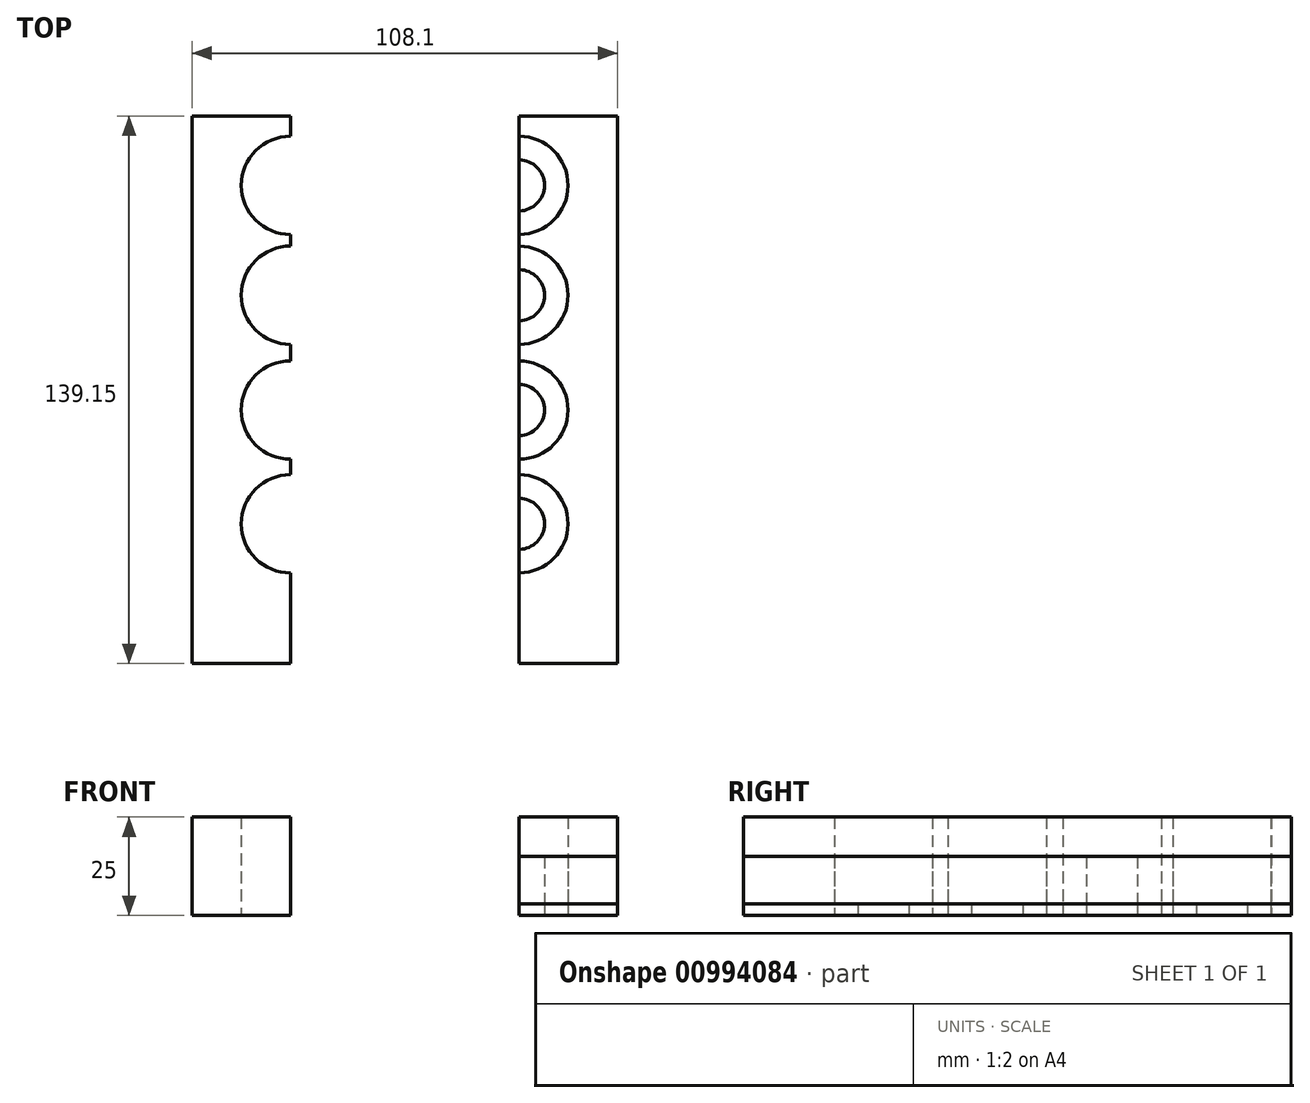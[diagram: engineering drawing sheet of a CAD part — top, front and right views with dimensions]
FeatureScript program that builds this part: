
annotation { "Feature Type Name" : "Feature", "Feature Type Description" : "" }
export const myFeature = defineFeature(function(context is Context, id is Id, definition is map)
    precondition{}
    {
        {
            var Q0;
            Q0=qCreatedBy(makeId("Top.planeOp"),FACE);
            var sketch = newSketch(context, id + "F0", { "sketchPlane" : qUnion([Q0])});
            skLineSegment(sketch, "E0.bottom", {"start": v(-54, 72.63) * mm, "end": v(54.1, 72.63) * mm});
            skLineSegment(sketch, "E0.top", {"start": v(-54, -66.52) * mm, "end": v(54.1, -66.52) * mm});
            skLineSegment(sketch, "E0.left", {"start": v(-54, 72.63) * mm, "end": v(-54, -66.52) * mm});
            skLineSegment(sketch, "E0.right", {"start": v(54.1, 72.63) * mm, "end": v(54.1, -66.52) * mm});
            skLineSegment(sketch, "E1.bottom", {"start": v(-54, 72.63) * mm, "end": v(-29, 72.63) * mm});
            skLineSegment(sketch, "E1.top", {"start": v(-54, -66.52) * mm, "end": v(-29, -66.52) * mm});
            skLineSegment(sketch, "E1.right", {"start": v(-29, 72.63) * mm, "end": v(-29, -66.52) * mm});
            skLineSegment(sketch, "E2.bottom", {"start": v(-29, 72.63) * mm, "end": v(0, 72.63) * mm});
            skLineSegment(sketch, "E2.top", {"start": v(-29, -66.52) * mm, "end": v(0, -66.52) * mm});
            skLineSegment(sketch, "E2.right", {"start": v(0, 72.63) * mm, "end": v(0, -66.52) * mm});
            skLineSegment(sketch, "E3.bottom", {"start": v(0, 72.63) * mm, "end": v(29.1, 72.63) * mm});
            skLineSegment(sketch, "E3.top", {"start": v(0, -66.52) * mm, "end": v(29.1, -66.52) * mm});
            skLineSegment(sketch, "E3.right", {"start": v(29.1, 72.63) * mm, "end": v(29.1, -66.52) * mm});
            skCircle(sketch, "E4", {"center": v(-29, 55) * mm, "radius": 12.5 * mm});
            skCircle(sketch, "E5", {"center": v(-29, 27.08) * mm, "radius": 12.5 * mm});
            skCircle(sketch, "E6", {"center": v(-29, -2.09) * mm, "radius": 12.5 * mm});
            skCircle(sketch, "E7", {"center": v(-29, -30.99) * mm, "radius": 12.5 * mm});
            skLineSegment(sketch, "E8.MirrorCS", {"start": v(0, 73.48) * mm, "end": v(0, -66.52) * mm});
            skCircle(sketch, "E9.MirrorC", {"center": v(29, 55) * mm, "radius": 12.5 * mm});
            skCircle(sketch, "E10.MirrorC", {"center": v(29, 27.08) * mm, "radius": 12.5 * mm});
            skCircle(sketch, "E11.MirrorC", {"center": v(29, -2.09) * mm, "radius": 12.5 * mm});
            skCircle(sketch, "E12.MirrorC", {"center": v(29, -30.99) * mm, "radius": 12.5 * mm});
            skCircle(sketch, "E13.MirrorC", {"center": v(0, 55) * mm, "radius": 12.5 * mm});
            skCircle(sketch, "E14.MirrorC", {"center": v(0, 27.08) * mm, "radius": 12.5 * mm});
            skCircle(sketch, "E15.MirrorC", {"center": v(0, -2.09) * mm, "radius": 12.5 * mm});
            skCircle(sketch, "E16.MirrorC", {"center": v(0, -30.99) * mm, "radius": 12.5 * mm});
            skCircle(sketch, "E17", {"center": v(-29, 55) * mm, "radius": 6.5 * mm});
            skCircle(sketch, "E18", {"center": v(-29, 27.08) * mm, "radius": 6.5 * mm});
            skCircle(sketch, "E19", {"center": v(-29, -2.09) * mm, "radius": 6.5 * mm});
            skCircle(sketch, "E20", {"center": v(-29, -30.99) * mm, "radius": 6.5 * mm});
            skCircle(sketch, "E21", {"center": v(0, -2.09) * mm, "radius": 6.5 * mm});
            skCircle(sketch, "E22", {"center": v(0, -30.99) * mm, "radius": 6.5 * mm});
            skCircle(sketch, "E23", {"center": v(0, 27.08) * mm, "radius": 6.5 * mm});
            skCircle(sketch, "E24", {"center": v(0, 55) * mm, "radius": 6.5 * mm});
            skCircle(sketch, "E25", {"center": v(29, 55) * mm, "radius": 6.5 * mm});
            skCircle(sketch, "E26", {"center": v(29, 27.08) * mm, "radius": 6.5 * mm});
            skCircle(sketch, "E27", {"center": v(29, -2.09) * mm, "radius": 6.5 * mm});
            skCircle(sketch, "E28", {"center": v(29, -30.99) * mm, "radius": 6.5 * mm});
            skSolve(sketch);
        }
        {
            var Q0;
            {var subQ4=sQuery(id+"F0.wireOp",EDGE,"E0.bottom");Q0=makeQuery(id+"F0.imprint","IMPRINT",FACE,{"disambiguationData":[TD([[makeQuery(id+"F0.imprint","IMPRINT",EDGE,{"derivedFrom":subQ4}),-1.0]])]});}
            extrude(context, id + "F1", {"entities" : qUnion([Q0]), "depth" : 25 * mm, "offsetDistance" : 25 * mm});
        }
        {
            var Q0;
            {var subQ0=sQuery(id+"F0.wireOp",EDGE,"E25");var subQ1=sQuery(id+"F0.wireOp",EDGE,"E3.right");var subQ2=makeQuery(id+"F0.imprint","INTERSECT",VERTEX,{"disambiguationData":[OD(0.0)],"derivedFrom":[subQ1,subQ0]});Q0=makeQuery(id+"F0.imprint","IMPRINT",FACE,{"disambiguationData":[TD([[makeQuery(id+"F0.imprint","IMPRINT",EDGE,{"disambiguationData":[TD([[subQ2,-1.0]])],"derivedFrom":subQ1}),1.0]])]});}
            var Q1;
            {var subQ0=sQuery(id+"F0.wireOp",EDGE,"E26");var subQ1=sQuery(id+"F0.wireOp",EDGE,"E3.right");var subQ2=makeQuery(id+"F0.imprint","INTERSECT",VERTEX,{"disambiguationData":[OD(0.0)],"derivedFrom":[subQ1,subQ0]});Q1=makeQuery(id+"F0.imprint","IMPRINT",FACE,{"disambiguationData":[TD([[makeQuery(id+"F0.imprint","IMPRINT",EDGE,{"disambiguationData":[TD([[subQ2,-1.0]])],"derivedFrom":subQ1}),1.0]])]});}
            var Q2;
            {var subQ0=sQuery(id+"F0.wireOp",EDGE,"E27");var subQ1=sQuery(id+"F0.wireOp",EDGE,"E3.right");var subQ2=makeQuery(id+"F0.imprint","INTERSECT",VERTEX,{"disambiguationData":[OD(0.0)],"derivedFrom":[subQ1,subQ0]});Q2=makeQuery(id+"F0.imprint","IMPRINT",FACE,{"disambiguationData":[TD([[makeQuery(id+"F0.imprint","IMPRINT",EDGE,{"disambiguationData":[TD([[subQ2,-1.0]])],"derivedFrom":subQ1}),1.0]])]});}
            var Q3;
            {var subQ0=sQuery(id+"F0.wireOp",EDGE,"E28");var subQ1=sQuery(id+"F0.wireOp",EDGE,"E3.right");var subQ2=makeQuery(id+"F0.imprint","INTERSECT",VERTEX,{"disambiguationData":[OD(0.0)],"derivedFrom":[subQ1,subQ0]});Q3=makeQuery(id+"F0.imprint","IMPRINT",FACE,{"disambiguationData":[TD([[makeQuery(id+"F0.imprint","IMPRINT",EDGE,{"disambiguationData":[TD([[subQ2,-1.0]])],"derivedFrom":subQ1}),1.0]])]});}
            extrude(context, id + "F2", {"entities" : qUnion([Q0, Q1, Q2, Q3]), "depth" : 3 * mm, "offsetDistance" : 25 * mm});
        }
        {
            var Q0;
            {var subQ0=sQuery(id+"F0.wireOp",EDGE,"E9.MirrorC");var subQ1=sQuery(id+"F0.wireOp",EDGE,"E3.right");var subQ2=makeQuery(id+"F0.imprint","INTERSECT",VERTEX,{"disambiguationData":[OD(0.0)],"derivedFrom":[subQ1,subQ0]});Q0=makeQuery(id+"F0.imprint","IMPRINT",FACE,{"disambiguationData":[TD([[makeQuery(id+"F0.imprint","IMPRINT",EDGE,{"disambiguationData":[TD([[subQ2,-1.0]])],"derivedFrom":subQ1}),1.0]])]});}
            var Q1;
            {var subQ0=sQuery(id+"F0.wireOp",EDGE,"E10.MirrorC");var subQ1=sQuery(id+"F0.wireOp",EDGE,"E3.right");var subQ2=makeQuery(id+"F0.imprint","INTERSECT",VERTEX,{"disambiguationData":[OD(0.0)],"derivedFrom":[subQ1,subQ0]});Q1=makeQuery(id+"F0.imprint","IMPRINT",FACE,{"disambiguationData":[TD([[makeQuery(id+"F0.imprint","IMPRINT",EDGE,{"disambiguationData":[TD([[subQ2,-1.0]])],"derivedFrom":subQ1}),1.0]])]});}
            var Q2;
            {var subQ0=sQuery(id+"F0.wireOp",EDGE,"E11.MirrorC");var subQ1=sQuery(id+"F0.wireOp",EDGE,"E3.right");var subQ2=makeQuery(id+"F0.imprint","INTERSECT",VERTEX,{"disambiguationData":[OD(0.0)],"derivedFrom":[subQ1,subQ0]});Q2=makeQuery(id+"F0.imprint","IMPRINT",FACE,{"disambiguationData":[TD([[makeQuery(id+"F0.imprint","IMPRINT",EDGE,{"disambiguationData":[TD([[subQ2,-1.0]])],"derivedFrom":subQ1}),1.0]])]});}
            var Q3;
            {var subQ0=sQuery(id+"F0.wireOp",EDGE,"E12.MirrorC");var subQ1=sQuery(id+"F0.wireOp",EDGE,"E3.right");var subQ2=makeQuery(id+"F0.imprint","INTERSECT",VERTEX,{"disambiguationData":[OD(0.0)],"derivedFrom":[subQ1,subQ0]});Q3=makeQuery(id+"F0.imprint","IMPRINT",FACE,{"disambiguationData":[TD([[makeQuery(id+"F0.imprint","IMPRINT",EDGE,{"disambiguationData":[TD([[subQ2,-1.0]])],"derivedFrom":subQ1}),1.0]])]});}
            extrude(context, id + "F3", {"entities" : qUnion([Q0, Q1, Q2, Q3]), "depth" : 15 * mm, "offsetDistance" : 25 * mm});
        }
        {
            var Q0;
            Q0=makeQuery(id+"F1.opExtrude","CAP_FACE",FACE,{"disambiguationData":[OSD([sQuery(id+"F0.wireOp",EDGE,"E0.bottom"),sQuery(id+"F0.wireOp",EDGE,"E0.top"),sQuery(id+"F0.wireOp",EDGE,"E0.right"),sQuery(id+"F0.wireOp",EDGE,"E3.right"),sQuery(id+"F0.wireOp",EDGE,"E9.MirrorC"),sQuery(id+"F0.wireOp",EDGE,"E10.MirrorC"),sQuery(id+"F0.wireOp",EDGE,"E11.MirrorC"),sQuery(id+"F0.wireOp",EDGE,"E12.MirrorC")])],"isStart":true});
            var sketch = newSketch(context, id + "F4", { "sketchPlane" : qUnion([Q0])});
            skLineSegment(sketch, "E29.bottom", {"start": v(29.1, 66.52) * mm, "end": v(54.1, 66.52) * mm});
            skLineSegment(sketch, "E29.top", {"start": v(29.1, -72.63) * mm, "end": v(54.1, -72.63) * mm});
            skLineSegment(sketch, "E29.left", {"start": v(29.1, 66.52) * mm, "end": v(29.1, -72.63) * mm});
            skLineSegment(sketch, "E29.right", {"start": v(54.1, 66.52) * mm, "end": v(54.1, -72.63) * mm});
            skSolve(sketch);
        }
        {
            var Q0;
            Q0 = qSketchRegion(id + "F4", true);
            extrude(context, id + "F5", {"entities" : qUnion([Q0]), "oppositeDirection" : true, "depth" : 3 * mm, "offsetDistance" : 25 * mm});
        }
    });
